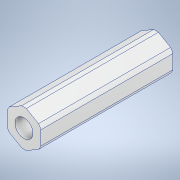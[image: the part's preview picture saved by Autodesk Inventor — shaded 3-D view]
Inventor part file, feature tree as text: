
AUTODESK INVENTOR PART (.ipt)
format: ipt  version: 2020 (Build 240168000, 168)  size: 118,272 bytes
history: native  units: in
note: dims shown in document units (in); Inventor stores cm internally (conversion verified against a paired STEP export)
features: extrude x1, sketch x1
ambient origin geometry x8: Origin, YZ Plane, XZ Plane, XY Plane, X Axis, Y Axis, Z Axis, Center Point
bodies: Solid1 (feature_tree)
feature tree (2):
  extrude  "Extrusion1"  Depth=1.95in
  sketch  "Sketch1"  dims[d0=0.5in d1=0.5413in d2=0.2656in d3=1.95in d4=0.0in]
